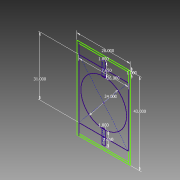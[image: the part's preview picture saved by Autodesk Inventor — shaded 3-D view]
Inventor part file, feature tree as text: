
AUTODESK INVENTOR PART (.ipt)
format: ipt  version: 2014 SP1 (Build 180222100, 222)  size: 82,944 bytes
history: native  units: in
note: dims shown in document units (in); Inventor stores cm internally (conversion verified against a paired STEP export)
features: sketch x1
ambient origin geometry x8: Origin, YZ Plane, XZ Plane, XY Plane, X Axis, Y Axis, Z Axis, Center Point
feature tree (1):
  sketch  "Sketch1"  dims[d2=1.8in d3=7.65in d4=1.8in d5=7.65in d7=24.0in d13=1.0in d14=26.0in d15=43.0in d16=28.0in d17=31.0in]
